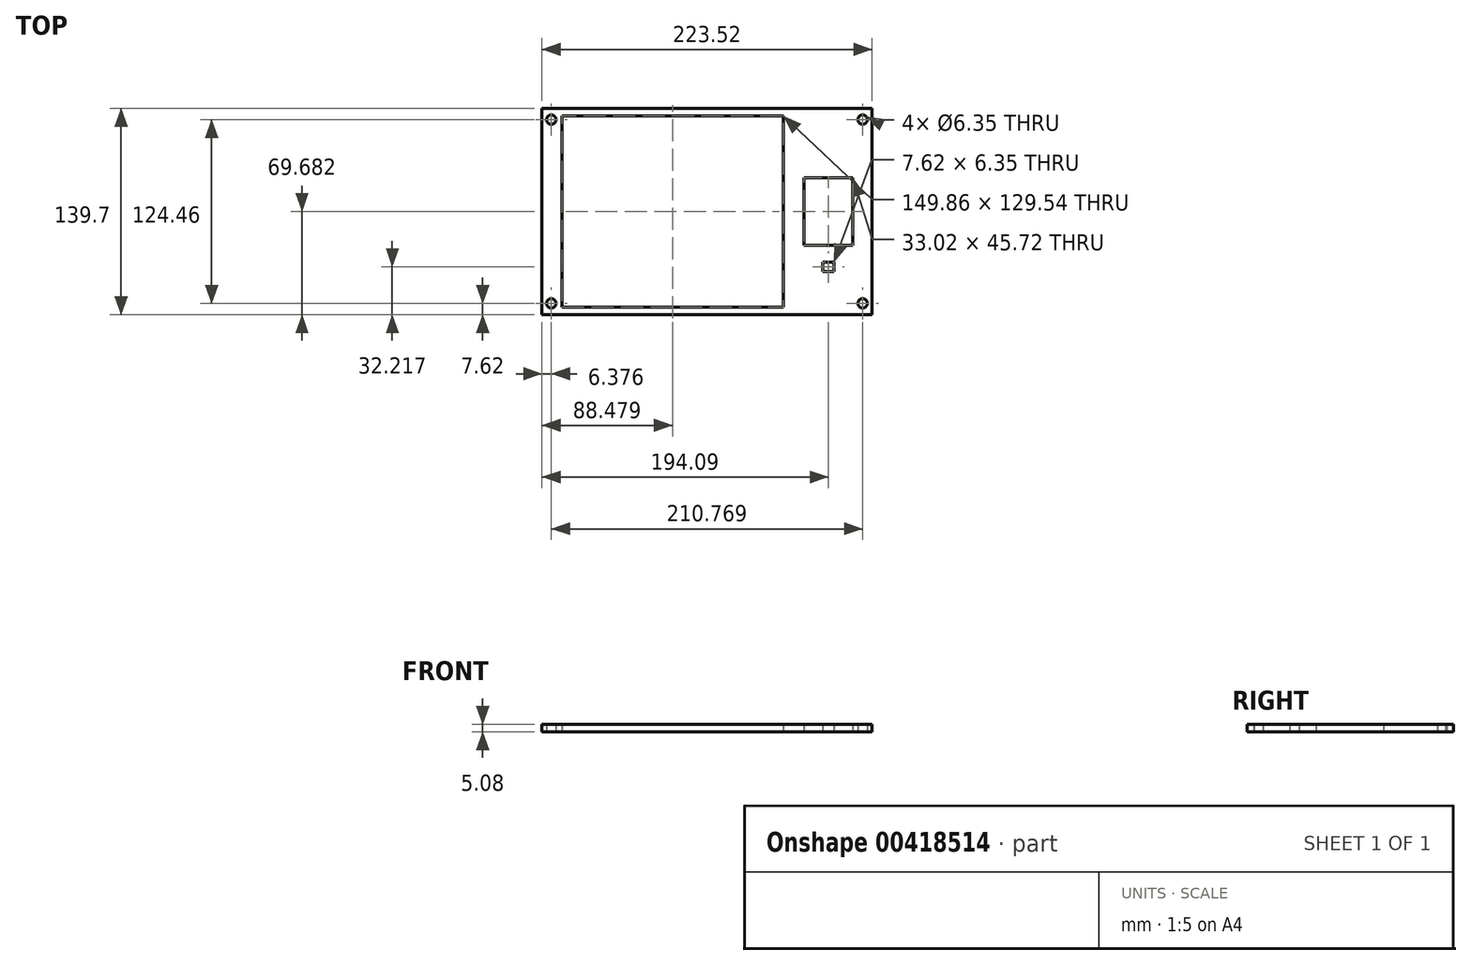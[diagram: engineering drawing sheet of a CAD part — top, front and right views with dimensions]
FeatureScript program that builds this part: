
annotation { "Feature Type Name" : "Feature", "Feature Type Description" : "" }
export const myFeature = defineFeature(function(context is Context, id is Id, definition is map)
    precondition{}
    {
        {
            var Q0;
            Q0=qCreatedBy(makeId("Top.planeOp"),FACE);
            var sketch = newSketch(context, id + "F0", { "sketchPlane" : qUnion([Q0])});
            skLineSegment(sketch, "E0.bottom", {"start": v(-196.78, 116.47) * mm, "end": v(20.81, 116.47) * mm});
            skLineSegment(sketch, "E0.top", {"start": v(-196.78, -23.23) * mm, "end": v(20.81, -23.23) * mm});
            skLineSegment(sketch, "E0.right", {"start": v(20.81, 116.47) * mm, "end": v(20.81, -23.23) * mm});
            skLineSegment(sketch, "E1.top", {"start": v(-196.78, 116.47) * mm, "end": v(-35.5, 116.47) * mm});
            skLineSegment(sketch, "E2.bottom", {"start": v(-35.5, 116.47) * mm, "end": v(-39.3, 116.47) * mm});
            skLineSegment(sketch, "E2.top", {"start": v(-35.5, 116.47) * mm, "end": v(-39.3, 116.47) * mm});
            skLineSegment(sketch, "E2.left", {"start": v(-35.5, 116.47) * mm, "end": v(-35.5, 116.47) * mm});
            skLineSegment(sketch, "E2.right", {"start": v(-39.3, 116.47) * mm, "end": v(-39.3, 116.47) * mm});
            skLineSegment(sketch, "E3", {"start": v(-196.78, 116.47) * mm, "end": v(-189.16, 116.47) * mm});
            skLineSegment(sketch, "E4.bottom", {"start": v(-189.16, 116.47) * mm, "end": v(-39.3, 116.47) * mm});
            skLineSegment(sketch, "E4.top", {"start": v(-189.16, 116.47) * mm, "end": v(-39.3, 116.47) * mm});
            skLineSegment(sketch, "E4.left", {"start": v(-189.16, 116.47) * mm, "end": v(-189.16, 116.47) * mm});
            skLineSegment(sketch, "E5.bottom", {"start": v(-189.16, 111.22) * mm, "end": v(-39.3, 111.22) * mm});
            skLineSegment(sketch, "E5.top", {"start": v(-189.16, -18.32) * mm, "end": v(-39.3, -18.32) * mm});
            skLineSegment(sketch, "E5.left", {"start": v(-189.16, 111.22) * mm, "end": v(-189.16, -18.32) * mm});
            skLineSegment(sketch, "E5.right", {"start": v(-39.3, 111.22) * mm, "end": v(-39.3, -18.32) * mm});
            skPoint(sketch, "E6.oppositeSnap0", {"position": v(-39.3, 46.45) * mm});
            skLineSegment(sketch, "E6.bottom", {"start": v(-35.5, 116.47) * mm, "end": v(15.3, 116.47) * mm});
            skLineSegment(sketch, "E7.bottom", {"start": v(-25.13, 69.31) * mm, "end": v(7.9, 69.31) * mm});
            skLineSegment(sketch, "E7.top", {"start": v(-25.13, 23.6) * mm, "end": v(7.9, 23.6) * mm});
            skLineSegment(sketch, "E7.left", {"start": v(-25.13, 69.31) * mm, "end": v(-25.13, 23.6) * mm});
            skLineSegment(sketch, "E7.right", {"start": v(7.9, 69.31) * mm, "end": v(7.9, 23.6) * mm});
            skLineSegment(sketch, "E8.bottom", {"start": v(-196.78, 116.47) * mm, "end": v(-202.7, 116.47) * mm});
            skLineSegment(sketch, "E8.top", {"start": v(-196.78, -23.23) * mm, "end": v(-202.7, -23.23) * mm});
            skLineSegment(sketch, "E8.right", {"start": v(-202.7, 116.47) * mm, "end": v(-202.7, -23.23) * mm});
            skLineSegment(sketch, "E9.bottom", {"start": v(-202.7, 116.47) * mm, "end": v(-195.09, 116.47) * mm});
            skLineSegment(sketch, "E9.left", {"start": v(-202.7, 116.47) * mm, "end": v(-202.7, 108.85) * mm});
            skCircle(sketch, "E10", {"center": v(-196.33, 108.85) * mm, "radius": 3.17 * mm});
            skLineSegment(sketch, "E11.bottom", {"start": v(-202.7, 116.47) * mm, "end": v(-187.47, 116.47) * mm});
            skLineSegment(sketch, "E11.left", {"start": v(-202.7, 116.47) * mm, "end": v(-202.7, 101.23) * mm});
            skLineSegment(sketch, "E12.left", {"start": v(-202.7, 101.23) * mm, "end": v(-202.7, -23.23) * mm});
            skLineSegment(sketch, "E13.bottom", {"start": v(-90.95, 111.4) * mm, "end": v(-189.16, 111.4) * mm});
            skLineSegment(sketch, "E13.top", {"start": v(-90.95, 116.47) * mm, "end": v(-187.47, 116.47) * mm});
            skLineSegment(sketch, "E14", {"start": v(-189.16, 111.4) * mm, "end": v(-189.16, 107.58) * mm});
            skPoint(sketch, "E15.visualSharp", {"position": v(-189.16, 101.23) * mm});
            skPoint(sketch, "E16.endSnap0", {"position": v(-87.98, -23.23) * mm});
            skCircle(sketch, "E17.MirrorC", {"center": v(14.43, 108.85) * mm, "radius": 3.17 * mm});
            skCircle(sketch, "E18.MirrorC", {"center": v(-196.33, -15.6) * mm, "radius": 3.17 * mm});
            skCircle(sketch, "E19.MirrorC", {"center": v(14.43, -15.6) * mm, "radius": 3.17 * mm});
            skPoint(sketch, "E20", {"position": v(-25.13, 46.45) * mm});
            skLineSegment(sketch, "E21", {"start": v(-25.13, 23.6) * mm, "end": v(-25.13, 5.81) * mm});
            skLineSegment(sketch, "E22.top", {"start": v(-25.13, 5.81) * mm, "end": v(7.9, 5.81) * mm});
            skLineSegment(sketch, "E22.right", {"start": v(7.9, 23.6) * mm, "end": v(7.9, 5.81) * mm});
            skPoint(sketch, "E23", {"position": v(-8.62, 5.81) * mm});
            skLineSegment(sketch, "E24.bottom", {"start": v(-8.62, 5.81) * mm, "end": v(-12.43, 5.81) * mm});
            skLineSegment(sketch, "E25", {"start": v(-12.43, 5.81) * mm, "end": v(-4.8, 5.81) * mm});
            skLineSegment(sketch, "E26.bottom", {"start": v(-4.8, 5.81) * mm, "end": v(-12.43, 5.81) * mm});
            skLineSegment(sketch, "E26.top", {"start": v(-4.8, 12.16) * mm, "end": v(-12.43, 12.16) * mm});
            skLineSegment(sketch, "E26.left", {"start": v(-4.8, 5.81) * mm, "end": v(-4.8, 12.16) * mm});
            skLineSegment(sketch, "E26.right", {"start": v(-12.43, 5.81) * mm, "end": v(-12.43, 12.16) * mm});
            skSolve(sketch);
        }
        {
            var Q0;
            Q0 = qSketchRegion(id + "F0", true);
            var Q1;
            Q1=makeQuery(id+"F0.imprint","IMPRINT",FACE,{"disambiguationData":[TD([[makeQuery(id+"F0.imprint","IMPRINT",EDGE,{"derivedFrom":sQuery(id+"F0.wireOp",EDGE,"E7.top")}),-1.0]])]});
            extrude(context, id + "F1", {"entities" : qUnion([Q0, Q1]), "depth" : 5.08 * mm, "offsetDistance" : 25.4 * mm});
        }
    });
